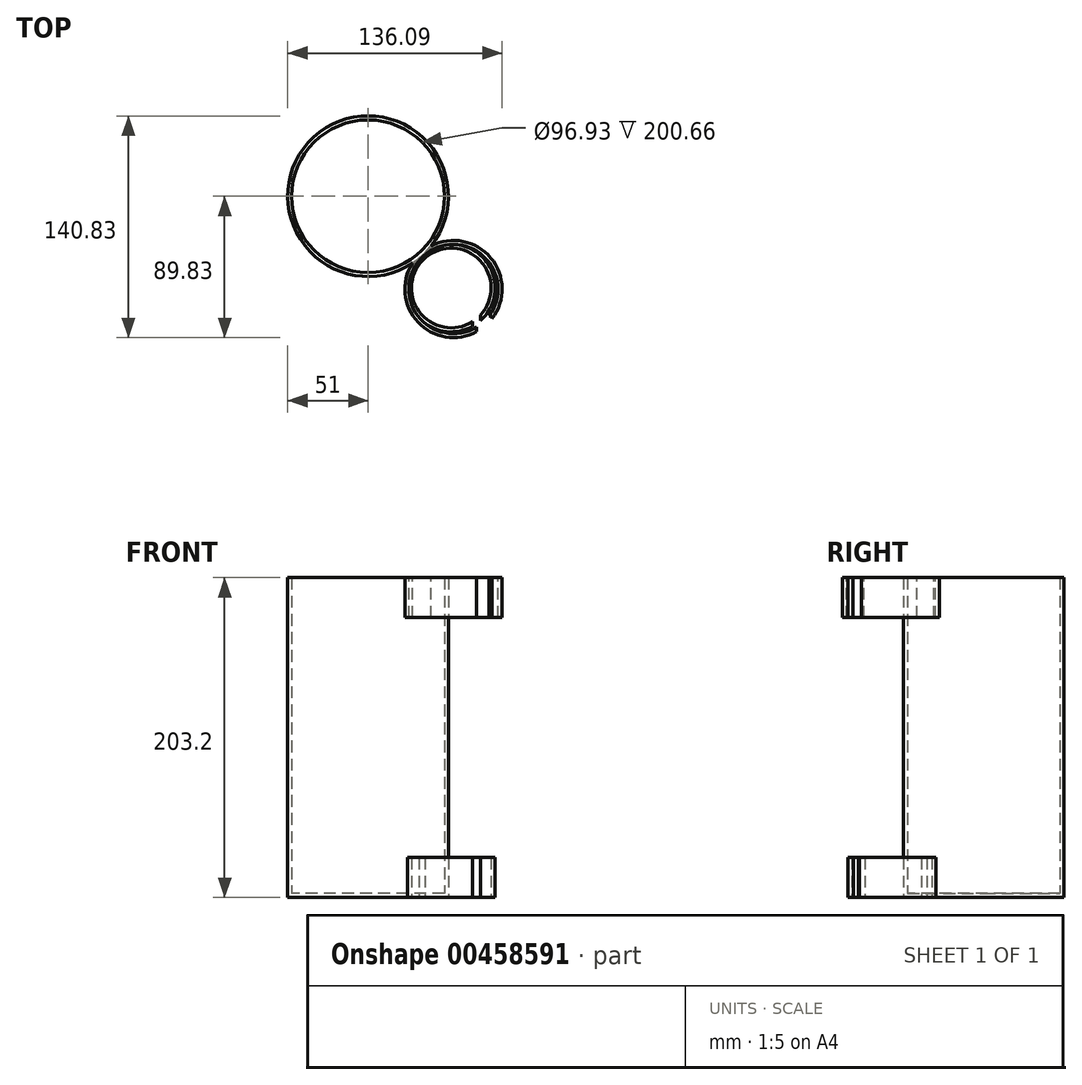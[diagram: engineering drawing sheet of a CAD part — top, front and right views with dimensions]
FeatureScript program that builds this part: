
annotation { "Feature Type Name" : "Feature", "Feature Type Description" : "" }
export const myFeature = defineFeature(function(context is Context, id is Id, definition is map)
    precondition{}
    {
        {
            var Q0;
            Q0=qCreatedBy(makeId("Top.planeOp"),FACE);
            var sketch = newSketch(context, id + "F0", { "sketchPlane" : qUnion([Q0])});
            skCircle(sketch, "E0", {"center": v(0, 0) * mm, "radius": 51 * mm});
            skSolve(sketch);
        }
        {
            var Q0;
            Q0 = qSketchRegion(id + "F0", true);
            extrude(context, id + "F1", {"entities" : qUnion([Q0]), "depth" : 203.2 * mm});
        }
        {
            var Q0;
            Q0=makeQuery(id+"F1.opExtrude","CAP_FACE",FACE,{"disambiguationData":[OSD([sQuery(id+"F0.wireOp",EDGE,"E0")])],"isStart":false});
            shell(context, id + "F2", {"entities" : qUnion([Q0]), "thickness" : 2.54 * mm});
        }
        {
            var Q0;
            Q0=makeQuery(id+"F1.opExtrude","CAP_FACE",FACE,{"disambiguationData":[OSD([sQuery(id+"F0.wireOp",EDGE,"E0")])],"isStart":false});
            var sketch = newSketch(context, id + "F3", { "sketchPlane" : qUnion([Q0])});
            skCircle(sketch, "E1", {"center": v(54.23, -58.98) * mm, "radius": 30.85 * mm});
            skSolve(sketch);
        }
        {
            var Q0;
            {var subQ0=sQuery(id+"F3.wireOp",EDGE,"E1");var subQ1=makeQuery(id+"F1.opExtrude","CAP_EDGE",EDGE,{"disambiguationData":[OSD([sQuery(id+"F0.wireOp",EDGE,"E0")])],"isStart":false});var subQ2=makeQuery(id+"F3.imprint","INTERSECT",VERTEX,{"disambiguationData":[OD(0.0)],"derivedFrom":[subQ1,subQ0]});Q0=makeQuery(id+"F3.imprint","IMPRINT",FACE,{"disambiguationData":[TD([[makeQuery(id+"F3.imprint","IMPRINT",EDGE,{"disambiguationData":[TD([[subQ2,1.0]])],"derivedFrom":subQ0}),1.0]])]});}
            var Q1;
            {var subQ0=sQuery(id+"F3.wireOp",EDGE,"E1");var subQ1=makeQuery(id+"F1.opExtrude","CAP_EDGE",EDGE,{"disambiguationData":[OSD([sQuery(id+"F0.wireOp",EDGE,"E0")])],"isStart":false});var subQ2=makeQuery(id+"F3.imprint","INTERSECT",VERTEX,{"disambiguationData":[OD(0.0)],"derivedFrom":[subQ1,subQ0]});Q1=makeQuery(id+"F3.imprint","IMPRINT",FACE,{"disambiguationData":[TD([[makeQuery(id+"F3.imprint","IMPRINT",EDGE,{"disambiguationData":[TD([[subQ2,-1.0]])],"derivedFrom":subQ0}),1.0]])]});}
            extrude(context, id + "F4", {"entities" : qUnion([Q0, Q1]), "operationType" : NewBodyOperationType.ADD, "oppositeDirection" : true, "depth" : 25.4 * mm});
        }
        {
            var Q0;
            Q0=makeQuery(id+"F4.opExtrude","CAP_FACE",FACE,{"disambiguationData":[OSD([sQuery(id+"F3.wireOp",EDGE,"E1")])],"isStart":false});
            shell(context, id + "F5", {"entities" : qUnion([Q0]), "thickness" : 2.54 * mm});
        }
        {
            var Q0;
            Q0=makeQuery(id+"F5.opShell","OFFSET_FACE",FACE,{"disambiguationData":[OSD([sQuery(id+"F0.wireOp",EDGE,"E0"),sQuery(id+"F3.wireOp",EDGE,"E1")])]});
            extrude(context, id + "F6", {"entities" : qUnion([Q0]), "operationType" : NewBodyOperationType.REMOVE, "oppositeDirection" : true, "depth" : 25.4 * mm});
        }
        {
            var Q0;
            Q0=makeQuery(id+"F4.boolean.opBoolean","MERGE",FACE,{"derivedFrom":[makeQuery(id+"F1.opExtrude","CAP_FACE",FACE,{"disambiguationData":[OSD([sQuery(id+"F0.wireOp",EDGE,"E0")])],"isStart":false}),makeQuery(id+"F4.opExtrude","CAP_FACE",FACE,{"disambiguationData":[OSD([sQuery(id+"F3.wireOp",EDGE,"E1")])],"isStart":true})]});
            var sketch = newSketch(context, id + "F7", { "sketchPlane" : qUnion([Q0])});
            skLineSegment(sketch, "E2.bottom", {"start": v(68.9, -76.17) * mm, "end": v(78.7, -76.17) * mm});
            skLineSegment(sketch, "E2.top", {"start": v(68.9, -88.06) * mm, "end": v(78.7, -88.06) * mm});
            skLineSegment(sketch, "E2.left", {"start": v(68.9, -76.17) * mm, "end": v(68.9, -88.06) * mm});
            skLineSegment(sketch, "E2.right", {"start": v(78.7, -76.17) * mm, "end": v(78.7, -88.06) * mm});
            skSolve(sketch);
        }
        {
            var Q0;
            Q0 = qSketchRegion(id + "F7", true);
            extrude(context, id + "F8", {"entities" : qUnion([Q0]), "operationType" : NewBodyOperationType.REMOVE, "oppositeDirection" : true, "depth" : 25.4 * mm});
        }
        {
            var Q0;
            Q0=makeQuery(id+"F1.opExtrude","CAP_FACE",FACE,{"disambiguationData":[OSD([sQuery(id+"F0.wireOp",EDGE,"E0")])],"isStart":true});
            var sketch = newSketch(context, id + "F9", { "sketchPlane" : qUnion([Q0])});
            skCircle(sketch, "E3", {"center": v(52.84, 58.3) * mm, "radius": 27.85 * mm});
            skSolve(sketch);
        }
        {
            var Q0;
            {var subQ0=sQuery(id+"F9.wireOp",EDGE,"E3");var subQ1=makeQuery(id+"F1.opExtrude","CAP_EDGE",EDGE,{"disambiguationData":[OSD([sQuery(id+"F0.wireOp",EDGE,"E0")])],"isStart":true});var subQ2=makeQuery(id+"F9.imprint","INTERSECT",VERTEX,{"disambiguationData":[OD(0.0)],"derivedFrom":[subQ1,subQ0]});Q0=makeQuery(id+"F9.imprint","IMPRINT",FACE,{"disambiguationData":[TD([[makeQuery(id+"F9.imprint","IMPRINT",EDGE,{"disambiguationData":[TD([[subQ2,1.0]])],"derivedFrom":subQ0}),1.0]])]});}
            extrude(context, id + "F10", {"entities" : qUnion([Q0]), "operationType" : NewBodyOperationType.ADD, "oppositeDirection" : true, "depth" : 25.4 * mm});
        }
        {
            var Q0;
            Q0=makeQuery(id+"F10.opExtrude","CAP_FACE",FACE,{"disambiguationData":[OSD([sQuery(id+"F0.wireOp",EDGE,"E0"),sQuery(id+"F9.wireOp",EDGE,"E3")])],"isStart":false});
            shell(context, id + "F11", {"entities" : qUnion([Q0]), "thickness" : 2.54 * mm});
        }
        {
            var Q0;
            Q0=makeQuery(id+"F11.opShell","OFFSET_FACE",FACE,{"disambiguationData":[OSD([sQuery(id+"F0.wireOp",EDGE,"E0"),sQuery(id+"F9.wireOp",EDGE,"E3")])]});
            extrude(context, id + "F12", {"entities" : qUnion([Q0]), "operationType" : NewBodyOperationType.REMOVE, "oppositeDirection" : true, "depth" : 25.4 * mm});
        }
        {
            var Q0;
            Q0=makeQuery(id+"F10.opExtrude","CAP_FACE",FACE,{"disambiguationData":[OSD([sQuery(id+"F0.wireOp",EDGE,"E0"),sQuery(id+"F9.wireOp",EDGE,"E3")])],"isStart":false});
            var sketch = newSketch(context, id + "F13", { "sketchPlane" : qUnion([Q0])});
            skPoint(sketch, "E4.firstSnap0", {"position": v(71.54, -78.94) * mm});
            skLineSegment(sketch, "E4.bottom", {"start": v(71.54, -85.34) * mm, "end": v(66.37, -85.34) * mm});
            skLineSegment(sketch, "E4.top", {"start": v(71.54, -70.9) * mm, "end": v(66.37, -70.9) * mm});
            skLineSegment(sketch, "E4.left", {"start": v(71.54, -85.34) * mm, "end": v(71.54, -70.9) * mm});
            skLineSegment(sketch, "E4.right", {"start": v(66.37, -85.34) * mm, "end": v(66.37, -70.9) * mm});
            skSolve(sketch);
        }
        {
            var Q0;
            Q0 = qSketchRegion(id + "F13", true);
            extrude(context, id + "F14", {"entities" : qUnion([Q0]), "operationType" : NewBodyOperationType.REMOVE, "oppositeDirection" : true, "depth" : 25.4 * mm});
        }
    });
